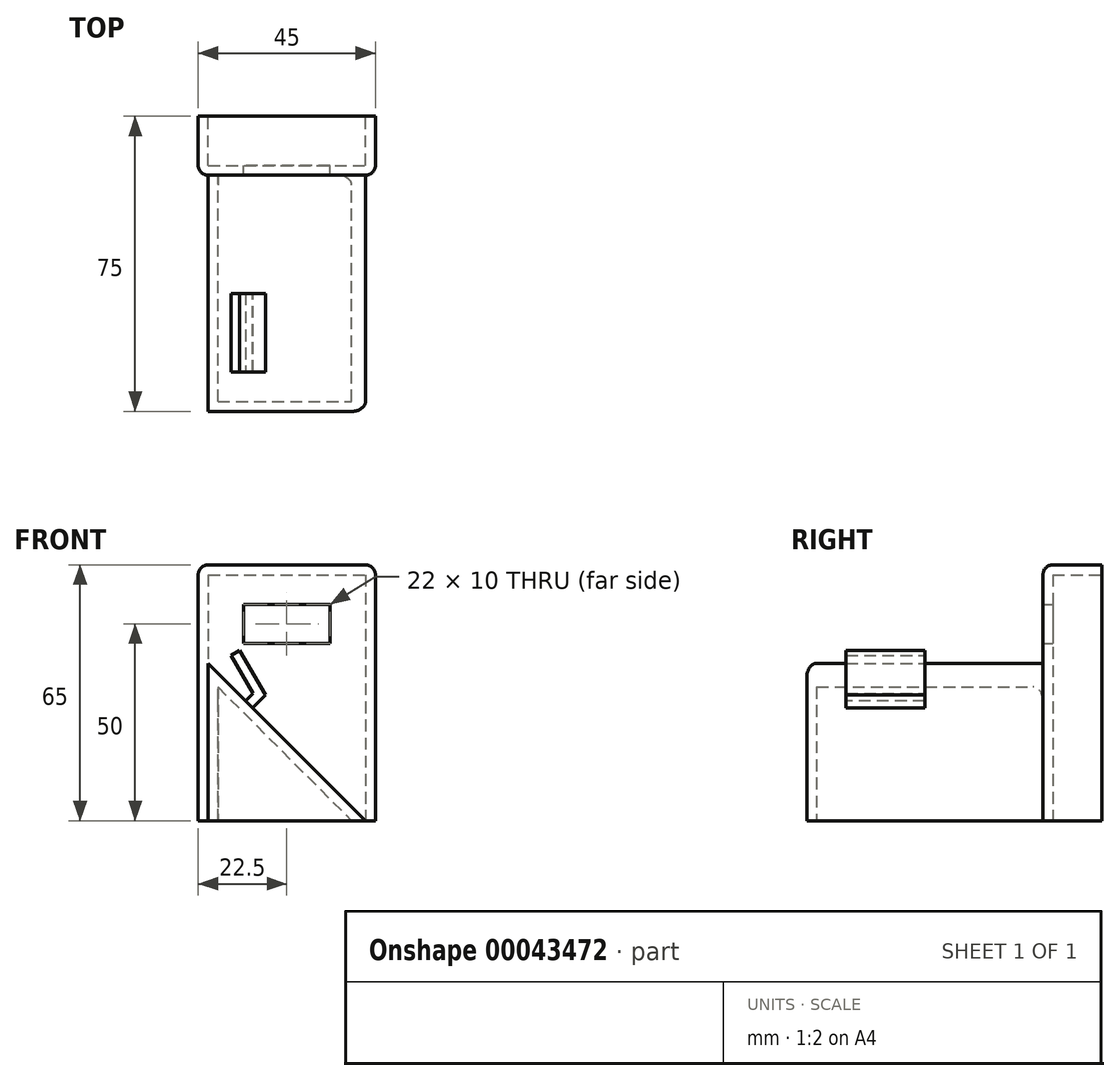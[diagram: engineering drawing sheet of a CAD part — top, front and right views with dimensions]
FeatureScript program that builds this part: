
annotation { "Feature Type Name" : "Feature", "Feature Type Description" : "" }
export const myFeature = defineFeature(function(context is Context, id is Id, definition is map)
    precondition{}
    {
        {
            var Q0;
            Q0=qCreatedBy(makeId("Front.planeOp"),FACE);
            var sketch = newSketch(context, id + "F0", { "sketchPlane" : qUnion([Q0])});
            skLineSegment(sketch, "E0.bottom", {"start": v(-22.5, 20) * mm, "end": v(22.5, 20) * mm});
            skLineSegment(sketch, "E0.top", {"start": v(-22.5, -45) * mm, "end": v(22.5, -45) * mm});
            skLineSegment(sketch, "E0.left", {"start": v(-22.5, 20) * mm, "end": v(-22.5, -45) * mm});
            skLineSegment(sketch, "E0.right", {"start": v(22.5, 20) * mm, "end": v(22.5, -45) * mm});
            skLineSegment(sketch, "E1", {"start": v(0, 0) * mm, "end": v(86.69, 0) * mm, "construction": true});
            skLineSegment(sketch, "E2", {"start": v(0, 0) * mm, "end": v(0, 75.34) * mm, "construction": true});
            skSolve(sketch);
        }
        {
            var Q0;
            Q0 = qSketchRegion(id + "F0", true);
            extrude(context, id + "F1", {"entities" : qUnion([Q0]), "depth" : 15 * mm});
        }
        {
            var Q0;
            Q0=makeQuery(id+"F1.opExtrude","CAP_EDGE",EDGE,{"disambiguationData":[OSD([sQuery(id+"F0.wireOp",EDGE,"E0.left")])],"isStart":false});
            var Q1;
            Q1=makeQuery(id+"F1.opExtrude","CAP_EDGE",EDGE,{"disambiguationData":[OSD([sQuery(id+"F0.wireOp",EDGE,"E0.bottom")])],"isStart":false});
            var Q2;
            Q2=makeQuery(id+"F1.opExtrude","CAP_EDGE",EDGE,{"disambiguationData":[OSD([sQuery(id+"F0.wireOp",EDGE,"E0.right")])],"isStart":false});
            var Q3;
            Q3=makeQuery(id+"F1.opExtrude","SWEPT_EDGE",EDGE,{"disambiguationData":[OSD([sQuery(id+"F0.wireOp",EDGE,"E0.bottom"),sQuery(id+"F0.wireOp",EDGE,"E0.right")])]});
            var Q4;
            Q4=makeQuery(id+"F1.opExtrude","SWEPT_EDGE",EDGE,{"disambiguationData":[OSD([sQuery(id+"F0.wireOp",EDGE,"E0.bottom"),sQuery(id+"F0.wireOp",EDGE,"E0.left")])]});
            fillet(context, id + "F2", {"entities" : qUnion([Q0, Q1, Q2, Q3, Q4]), "radius" : 2.5 * mm, "tangentPropagation" : true, "allowEdgeOverflow" : false});
        }
        {
            var Q0;
            Q0=makeQuery(id+"F1.opExtrude","SWEPT_FACE",FACE,{"disambiguationData":[OSD([sQuery(id+"F0.wireOp",EDGE,"E0.top")])]});
            var Q1;
            Q1=makeQuery(id+"F1.opExtrude","CAP_FACE",FACE,{"disambiguationData":[OSD([sQuery(id+"F0.wireOp",EDGE,"E0.bottom"),sQuery(id+"F0.wireOp",EDGE,"E0.top"),sQuery(id+"F0.wireOp",EDGE,"E0.left"),sQuery(id+"F0.wireOp",EDGE,"E0.right")])],"isStart":true});
            shell(context, id + "F3", {"entities" : qUnion([Q0, Q1]), "thickness" : 2.5 * mm});
        }
        {
            var Q0;
            Q0=qCreatedBy(makeId("Front.planeOp"),FACE);
            var sketch = newSketch(context, id + "F4", { "sketchPlane" : qUnion([Q0])});
            skLineSegment(sketch, "E3.bottom", {"start": v(-11, 0) * mm, "end": v(11, 0) * mm});
            skLineSegment(sketch, "E3.top", {"start": v(-11, 10) * mm, "end": v(11, 10) * mm});
            skLineSegment(sketch, "E3.left", {"start": v(-11, 0) * mm, "end": v(-11, 10) * mm});
            skLineSegment(sketch, "E3.right", {"start": v(11, 0) * mm, "end": v(11, 10) * mm});
            skLineSegment(sketch, "E4", {"start": v(0, 0) * mm, "end": v(0, 31.36) * mm, "construction": true});
            skSolve(sketch);
        }
        {
            var Q0;
            Q0 = qSketchRegion(id + "F4", true);
            extrude(context, id + "F5", {"entities" : qUnion([Q0]), "operationType" : NewBodyOperationType.REMOVE, "depth" : 25 * mm});
        }
        {
            var Q0;
            Q0=makeQuery(id+"F1.opExtrude","CAP_FACE",FACE,{"disambiguationData":[OSD([sQuery(id+"F0.wireOp",EDGE,"E0.bottom"),sQuery(id+"F0.wireOp",EDGE,"E0.top"),sQuery(id+"F0.wireOp",EDGE,"E0.left"),sQuery(id+"F0.wireOp",EDGE,"E0.right")])],"isStart":false});
            var sketch = newSketch(context, id + "F6", { "sketchPlane" : qUnion([Q0])});
            skLineSegment(sketch, "E5", {"start": v(-20, -45) * mm, "end": v(-20, -5) * mm});
            skLineSegment(sketch, "E6", {"start": v(-20, -5) * mm, "end": v(20, -45) * mm});
            skLineSegment(sketch, "E7", {"start": v(20, -45) * mm, "end": v(-20, -45) * mm});
            skLineSegment(sketch, "E8", {"start": v(0, 0) * mm, "end": v(0, -57.51) * mm, "construction": true});
            skSolve(sketch);
        }
        {
            var Q0;
            Q0 = qSketchRegion(id + "F6", true);
            extrude(context, id + "F7", {"entities" : qUnion([Q0]), "operationType" : NewBodyOperationType.ADD, "depth" : 60 * mm});
        }
        {
            var Q0;
            Q0=makeQuery(id+"F7.boolean.opBoolean","MERGE",FACE,{"derivedFrom":[makeQuery(id+"F1.opExtrude","SWEPT_FACE",FACE,{"disambiguationData":[OSD([sQuery(id+"F0.wireOp",EDGE,"E0.top")])]}),makeQuery(id+"F7.opExtrude","SWEPT_FACE",FACE,{"disambiguationData":[OSD([sQuery(id+"F6.wireOp",EDGE,"E7")])]})]});
            shell(context, id + "F8", {"entities" : qUnion([Q0]), "thickness" : 2.5 * mm});
        }
        {
            var Q0;
            Q0=makeQuery(id+"F7.opExtrude","CAP_EDGE",EDGE,{"disambiguationData":[OSD([sQuery(id+"F6.wireOp",EDGE,"E6")])],"isStart":true});
            var Q1;
            Q1=makeQuery(id+"F7.opExtrude","CAP_EDGE",EDGE,{"disambiguationData":[OSD([sQuery(id+"F6.wireOp",EDGE,"E6")])],"isStart":false});
            var Q2;
            Q2=makeQuery(id+"F8.opShell","TWEAK_EDGE",EDGE,{"derivedFrom":[makeQuery(id+"F3.opShell","OFFSET_FACE",FACE,{"disambiguationData":[OSD([sQuery(id+"F0.wireOp",EDGE,"E0.bottom"),sQuery(id+"F0.wireOp",EDGE,"E0.top"),sQuery(id+"F0.wireOp",EDGE,"E0.left"),sQuery(id+"F0.wireOp",EDGE,"E0.right")])]}),makeQuery(id+"F7.opExtrude","SWEPT_FACE",FACE,{"disambiguationData":[OSD([sQuery(id+"F6.wireOp",EDGE,"E6")])]})]});
            fillet(context, id + "F9", {"entities" : qUnion([Q0, Q1, Q2]), "radius" : 2.5 * mm, "tangentPropagation" : true, "allowEdgeOverflow" : false});
        }
        {
            var Q0;
            Q0=makeQuery(id+"F7.opExtrude","CAP_FACE",FACE,{"disambiguationData":[OSD([sQuery(id+"F6.wireOp",EDGE,"E5"),sQuery(id+"F6.wireOp",EDGE,"E6"),sQuery(id+"F6.wireOp",EDGE,"E7")])],"isStart":false});
            cPlane(context, id + "F10", {"entities" : qUnion([Q0]), "cplaneType" : CPlaneType.OFFSET, "offset" : 20 * mm, "oppositeDirection" : true, "width" : 150 * mm, "height" : 150 * mm});
        }
        {
            var Q0;
            Q0=qCreatedBy(id+"F10.planeOp",FACE);
            var sketch = newSketch(context, id + "F11", { "sketchPlane" : qUnion([Q0])});
            skLineSegment(sketch, "E9", {"start": v(-18.14, -6.86) * mm, "end": v(22.88, -47.88) * mm, "construction": true});
            skLineSegment(sketch, "E10", {"start": v(-11.51, -15.6) * mm, "end": v(-8.55, -12.64) * mm});
            skLineSegment(sketch, "E11", {"start": v(-8.55, -12.64) * mm, "end": v(-14.14, -2.97) * mm});
            skLineSegment(sketch, "E12", {"start": v(-14.14, -2.97) * mm, "end": v(-11.97, -1.72) * mm});
            skLineSegment(sketch, "E13", {"start": v(-11.97, -1.72) * mm, "end": v(-5.43, -13.05) * mm});
            skLineSegment(sketch, "E14", {"start": v(-5.43, -13.05) * mm, "end": v(-9.75, -17.37) * mm});
            skLineSegment(sketch, "E15", {"start": v(-9.75, -17.37) * mm, "end": v(-11.51, -15.6) * mm});
            skSolve(sketch);
        }
        {
            var Q0;
            Q0 = qSketchRegion(id + "F11", true);
            extrude(context, id + "F12", {"entities" : qUnion([Q0]), "operationType" : NewBodyOperationType.ADD, "endBound" : BoundingType.SYMMETRIC, "depth" : 20 * mm});
        }
    });
